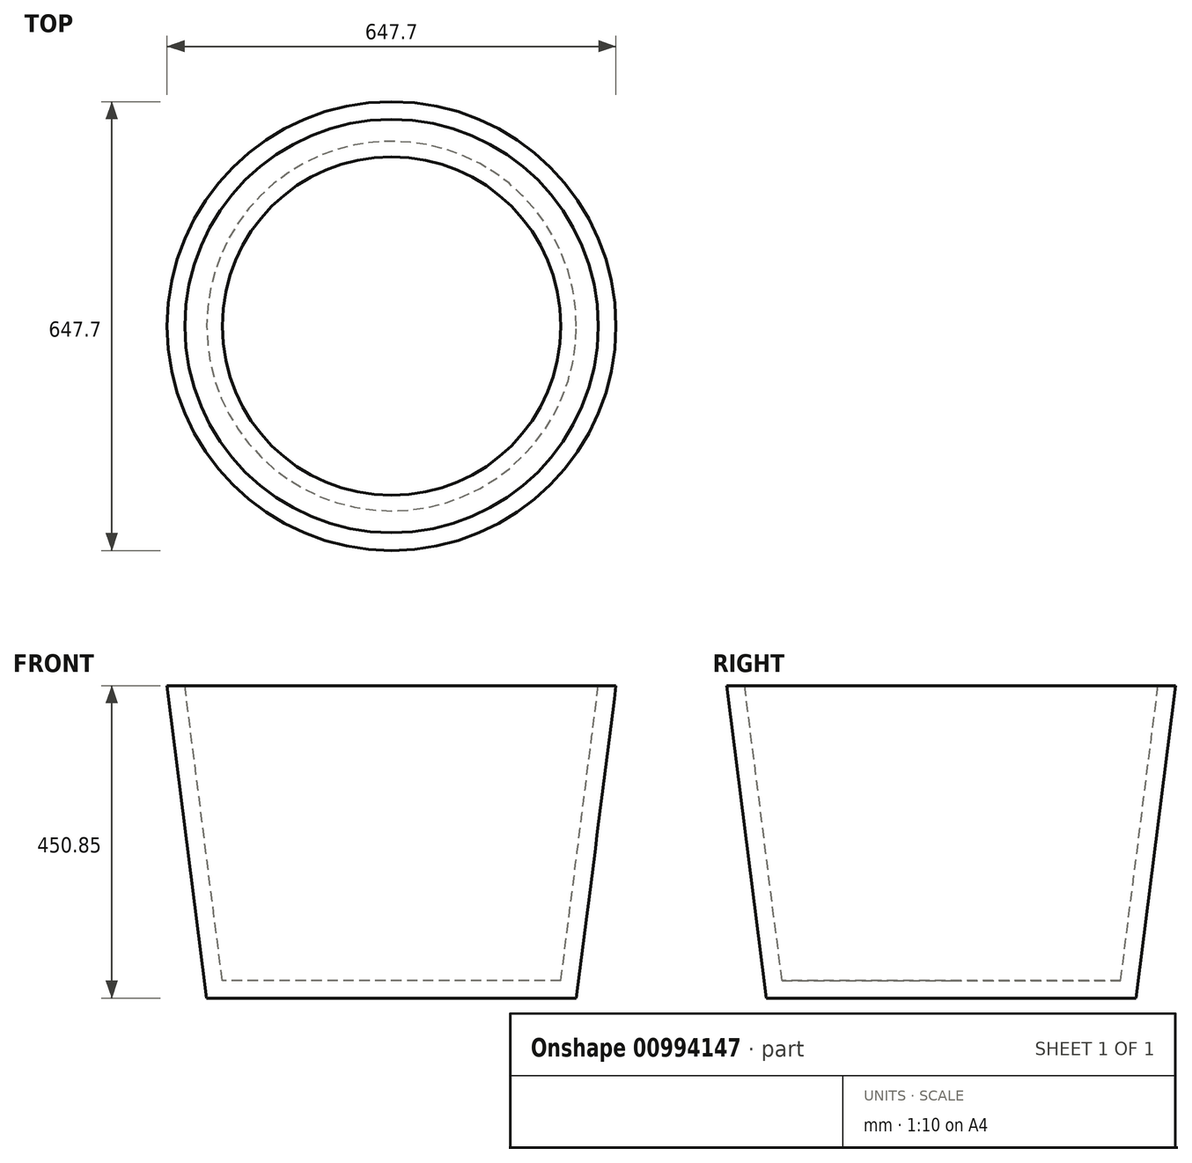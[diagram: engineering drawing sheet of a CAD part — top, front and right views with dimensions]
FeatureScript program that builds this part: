
annotation { "Feature Type Name" : "Feature", "Feature Type Description" : "" }
export const myFeature = defineFeature(function(context is Context, id is Id, definition is map)
    precondition{}
    {
        {
            var Q0;
            Q0=qCreatedBy(makeId("Top.planeOp"),FACE);
            var sketch = newSketch(context, id + "F0", { "sketchPlane" : qUnion([Q0])});
            skCircle(sketch, "E0", {"center": v(0, 0) * mm, "radius": 323.85 * mm});
            skSolve(sketch);
        }
        {
            var Q0;
            Q0=makeQuery(id+"F0.imprint","IMPRINT",FACE,{"disambiguationData":[TD([[makeQuery(id+"F0.imprint","IMPRINT",EDGE,{"derivedFrom":sQuery(id+"F0.wireOp",EDGE,"E0")}),1.0]])]});
            cPlane(context, id + "F1", {"entities" : qUnion([Q0]), "cplaneType" : CPlaneType.OFFSET, "offset" : 450.85 * mm, "oppositeDirection" : true, "width" : 152.4 * mm, "height" : 152.4 * mm});
        }
        {
            var Q0;
            Q0=qCreatedBy(id+"F1.planeOp",FACE);
            var sketch = newSketch(context, id + "F2", { "sketchPlane" : qUnion([Q0])});
            skCircle(sketch, "E1", {"center": v(0, 0) * mm, "radius": 266.7 * mm});
            skSolve(sketch);
        }
        {
            var Q0;
            Q0=makeQuery(id+"F2.imprint","IMPRINT",FACE,{"disambiguationData":[TD([[makeQuery(id+"F2.imprint","IMPRINT",EDGE,{"derivedFrom":sQuery(id+"F2.wireOp",EDGE,"E1")}),1.0]])]});
            var Q1;
            Q1=makeQuery(id+"F0.imprint","IMPRINT",FACE,{"disambiguationData":[TD([[makeQuery(id+"F0.imprint","IMPRINT",EDGE,{"derivedFrom":sQuery(id+"F0.wireOp",EDGE,"E0")}),1.0]])]});
            loft(context, id + "F3", {"sheetProfilesArray" : [{ "sheetProfileEntities" : qUnion([Q0]) }, { "sheetProfileEntities" : qUnion([Q1]) }]});
        }
        {
            var Q0;
            Q0=makeQuery(id+"F3.opLoft","CAP_FACE",FACE,{"disambiguationData":[OSD([makeQuery(id+"F0.imprint","IMPRINT",FACE,{"disambiguationData":[TD([[makeQuery(id+"F0.imprint","IMPRINT",EDGE,{"derivedFrom":sQuery(id+"F0.wireOp",EDGE,"E0")}),1.0]])]})])],"isStart":true});
            shell(context, id + "F4", {"entities" : qUnion([Q0]), "thickness" : 25.4 * mm});
        }
    });
